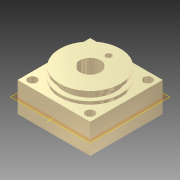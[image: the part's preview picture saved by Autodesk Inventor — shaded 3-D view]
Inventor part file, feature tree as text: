
AUTODESK INVENTOR PART (.ipt)
format: ipt  version: 2011 (Build 150229000, 229)  size: 152,576 bytes
history: native  units: mm
features: sketch x5, hole x4, extrude x1, pattern_linear x1, revolve x1, plane x1, other x1
ambient origin geometry x8: Origin, YZ Plane, XZ Plane, XY Plane, X Axis, Y Axis, Z Axis, Center Point
feature tree (14):
  extrude  "Extrusion1"  Depth=5.0mm
  hole  "Hole1"  [1 undecoded]
  pattern_linear  "Rectangular Pattern1"  Count1=2 Spacing1=39.0mm
  revolve  "Revolution1"  [1 undecoded]
  hole  "Hole4"  [1 undecoded]
  plane  "Work Plane3"
  hole  "Hole5"  [1 undecoded]
  hole  "Hole6"  [1 undecoded]
  sketch  "Sketch1"  dims[d2=20.0mm d3=0.0mm d4=5.0mm]
  sketch  "Sketch2"  dims[d5=39.0mm d6=39.0mm]
  sketch  "Sketch3"  dims[d7=6.0mm d8=6.0mm d9=4.0mm d10=2.0mm d11=90.0deg d12=8.0mm d13=20.594885mm d14=20.0mm d16=39.0mm]
  sketch  "Sketch4"  dims[d17=20.0mm d19=39.0mm d25=8.0mm]
  other  "Work Axis2"
  sketch  "Sketch7"  dims[d26=20.5mm d27=2.0mm d28=4.0mm d29=17.5mm d30=90.0deg d31=10.0mm d48=4.134mm d49=6.0mm d50=4.0mm d51=2.0mm d52=90.0deg d53=14.0mm d54=20.594885mm d55=0.0mm d56=12.5mm d57=4.0mm d58=6.0mm d59=4.0mm d60=2.0mm d61=90.0deg d62=14.0mm d63=20.594885mm d64=10.0mm d65=10.0mm d66=14.0mm d67=6.0mm d68=4.0mm d69=2.0mm d70=90.0deg d71=14.0mm d72=20.594885mm]
note: 5 required parameter values undecoded (feature->parameter linkage not recoverable at this tier; creation-order binding heuristic only, values carry confidence <= 0.55)